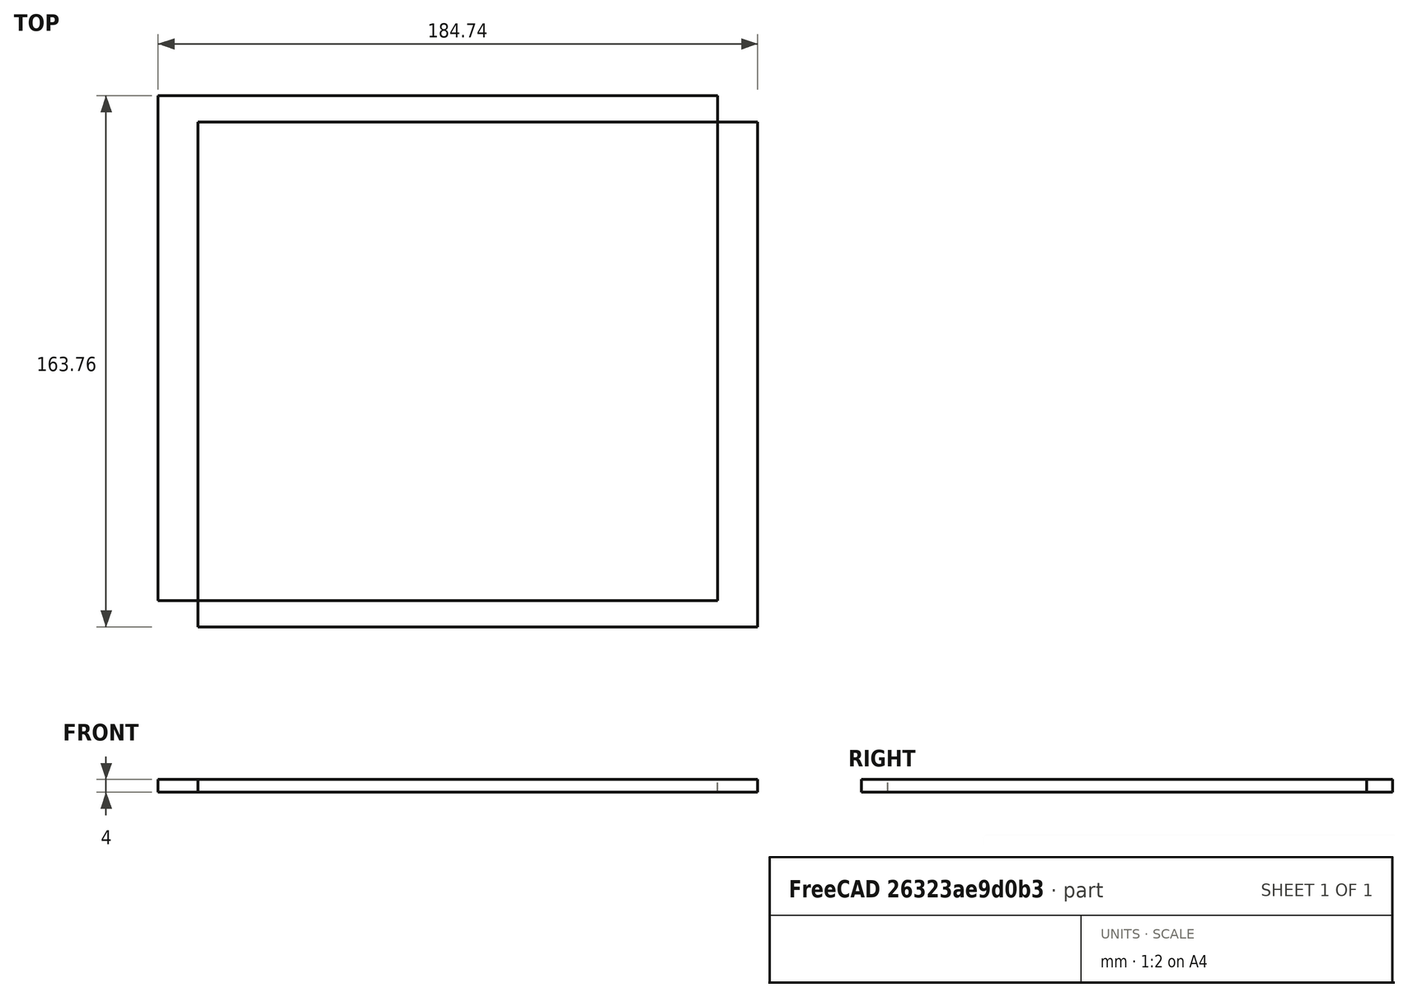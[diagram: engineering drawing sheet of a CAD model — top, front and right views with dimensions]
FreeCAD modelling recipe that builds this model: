
FCSTD DOCUMENT  (FreeCAD 0.19R22922 (Git))
Label: base
License: All rights reserved
LicenseURL: http://en.wikipedia.org/wiki/All_rights_reserved
objects: Path::FeaturePython×6, Sketcher::SketchObject×4, Part::FeaturePython×3, PartDesign::Pad×2, PartDesign::Pocket×2, Part::Feature×1, PartDesign::Fillet×1, PartDesign::Body×1, App::FeaturePython×1, App::DocumentObjectGroup×1, Path::FeatureCompoundPython×1, Mesh::FeaturePython×1
note: 21 computed .brp shape members not serialized (recipe doc carries the construction recipe); baked Part::Feature solids carry a one-line shape summary decoded from their .brp

FEATURE [Part::Feature] path888
  shape: bbox 153.6 x 170.4 x 2e-07 mm, 1 faces, 0 solids (baked)
FEATURE [Sketcher::SketchObject] Sketch
  MapMode = 5
  Support = -> [XY_Plane]
  sketch-geometry (193):
    g0: BSplineCurve PolesCount=2 KnotsCount=2 Degree=1 IsPeriodic=0
    g1: BSplineCurve PolesCount=2 KnotsCount=2 Degree=1 IsPeriodic=0
    g2: BSplineCurve PolesCount=2 KnotsCount=2 Degree=1 IsPeriodic=0
    g3: BSplineCurve PolesCount=2 KnotsCount=2 Degree=1 IsPeriodic=0
    g4: BSplineCurve PolesCount=2 KnotsCount=2 Degree=1 IsPeriodic=0
    g5: BSplineCurve PolesCount=2 KnotsCount=2 Degree=1 IsPeriodic=0
    g6: BSplineCurve PolesCount=2 KnotsCount=2 Degree=1 IsPeriodic=0
    g7: BSplineCurve PolesCount=2 KnotsCount=2 Degree=1 IsPeriodic=0
    g8: BSplineCurve PolesCount=2 KnotsCount=2 Degree=1 IsPeriodic=0
    g9: BSplineCurve PolesCount=2 KnotsCount=2 Degree=1 IsPeriodic=0
    g10: BSplineCurve PolesCount=2 KnotsCount=2 Degree=1 IsPeriodic=0
    g11: BSplineCurve PolesCount=2 KnotsCount=2 Degree=1 IsPeriodic=0
    g12: BSplineCurve PolesCount=2 KnotsCount=2 Degree=1 IsPeriodic=0
    g13: BSplineCurve PolesCount=2 KnotsCount=2 Degree=1 IsPeriodic=0
    g14: BSplineCurve PolesCount=2 KnotsCount=2 Degree=1 IsPeriodic=0
    g15: BSplineCurve PolesCount=2 KnotsCount=2 Degree=1 IsPeriodic=0
    g16: BSplineCurve PolesCount=2 KnotsCount=2 Degree=1 IsPeriodic=0
    g17: BSplineCurve PolesCount=2 KnotsCount=2 Degree=1 IsPeriodic=0
    g18: BSplineCurve PolesCount=2 KnotsCount=2 Degree=1 IsPeriodic=0
    g19: BSplineCurve PolesCount=2 KnotsCount=2 Degree=1 IsPeriodic=0
    g20: BSplineCurve PolesCount=2 KnotsCount=2 Degree=1 IsPeriodic=0
    g21: BSplineCurve PolesCount=2 KnotsCount=2 Degree=1 IsPeriodic=0
    g22: BSplineCurve PolesCount=2 KnotsCount=2 Degree=1 IsPeriodic=0
    g23: BSplineCurve PolesCount=2 KnotsCount=2 Degree=1 IsPeriodic=0
    g24: BSplineCurve PolesCount=2 KnotsCount=2 Degree=1 IsPeriodic=0
    g25: BSplineCurve PolesCount=2 KnotsCount=2 Degree=1 IsPeriodic=0
    g26: BSplineCurve PolesCount=2 KnotsCount=2 Degree=1 IsPeriodic=0
    g27: BSplineCurve PolesCount=2 KnotsCount=2 Degree=1 IsPeriodic=0
    g28: BSplineCurve PolesCount=2 KnotsCount=2 Degree=1 IsPeriodic=0
    g29: BSplineCurve PolesCount=2 KnotsCount=2 Degree=1 IsPeriodic=0
    g30: BSplineCurve PolesCount=2 KnotsCount=2 Degree=1 IsPeriodic=0
    g31: BSplineCurve PolesCount=2 KnotsCount=2 Degree=1 IsPeriodic=0
    g32: BSplineCurve PolesCount=2 KnotsCount=2 Degree=1 IsPeriodic=0
    g33: BSplineCurve PolesCount=2 KnotsCount=2 Degree=1 IsPeriodic=0
    g34: BSplineCurve PolesCount=2 KnotsCount=2 Degree=1 IsPeriodic=0
    g35: BSplineCurve PolesCount=2 KnotsCount=2 Degree=1 IsPeriodic=0
    g36: BSplineCurve PolesCount=2 KnotsCount=2 Degree=1 IsPeriodic=0
    g37: BSplineCurve PolesCount=2 KnotsCount=2 Degree=1 IsPeriodic=0
    g38: BSplineCurve PolesCount=2 KnotsCount=2 Degree=1 IsPeriodic=0
    g39: BSplineCurve PolesCount=2 KnotsCount=2 Degree=1 IsPeriodic=0
    g40: BSplineCurve PolesCount=2 KnotsCount=2 Degree=1 IsPeriodic=0
    g41: BSplineCurve PolesCount=2 KnotsCount=2 Degree=1 IsPeriodic=0
    g42: BSplineCurve PolesCount=2 KnotsCount=2 Degree=1 IsPeriodic=0
    g43: BSplineCurve PolesCount=2 KnotsCount=2 Degree=1 IsPeriodic=0
    g44: BSplineCurve PolesCount=2 KnotsCount=2 Degree=1 IsPeriodic=0
    g45: BSplineCurve PolesCount=2 KnotsCount=2 Degree=1 IsPeriodic=0
    g46: BSplineCurve PolesCount=2 KnotsCount=2 Degree=1 IsPeriodic=0
    g47: BSplineCurve PolesCount=2 KnotsCount=2 Degree=1 IsPeriodic=0
    g48: BSplineCurve PolesCount=2 KnotsCount=2 Degree=1 IsPeriodic=0
    g49: BSplineCurve PolesCount=2 KnotsCount=2 Degree=1 IsPeriodic=0
    g50: BSplineCurve PolesCount=2 KnotsCount=2 Degree=1 IsPeriodic=0
    g51: BSplineCurve PolesCount=2 KnotsCount=2 Degree=1 IsPeriodic=0
    g52: BSplineCurve PolesCount=2 KnotsCount=2 Degree=1 IsPeriodic=0
    g53: BSplineCurve PolesCount=2 KnotsCount=2 Degree=1 IsPeriodic=0
    g54: BSplineCurve PolesCount=2 KnotsCount=2 Degree=1 IsPeriodic=0
    g55: BSplineCurve PolesCount=2 KnotsCount=2 Degree=1 IsPeriodic=0
    g56: BSplineCurve PolesCount=2 KnotsCount=2 Degree=1 IsPeriodic=0
    g57: BSplineCurve PolesCount=2 KnotsCount=2 Degree=1 IsPeriodic=0
    g58: BSplineCurve PolesCount=2 KnotsCount=2 Degree=1 IsPeriodic=0
    g59: BSplineCurve PolesCount=2 KnotsCount=2 Degree=1 IsPeriodic=0
    g60: BSplineCurve PolesCount=2 KnotsCount=2 Degree=1 IsPeriodic=0
    g61: BSplineCurve PolesCount=2 KnotsCount=2 Degree=1 IsPeriodic=0
    g62: BSplineCurve PolesCount=2 KnotsCount=2 Degree=1 IsPeriodic=0
    g63: BSplineCurve PolesCount=2 KnotsCount=2 Degree=1 IsPeriodic=0
    g64: BSplineCurve PolesCount=2 KnotsCount=2 Degree=1 IsPeriodic=0
    g65: BSplineCurve PolesCount=2 KnotsCount=2 Degree=1 IsPeriodic=0
    g66: BSplineCurve PolesCount=2 KnotsCount=2 Degree=1 IsPeriodic=0
    g67: BSplineCurve PolesCount=2 KnotsCount=2 Degree=1 IsPeriodic=0
    g68: BSplineCurve PolesCount=2 KnotsCount=2 Degree=1 IsPeriodic=0
    g69: BSplineCurve PolesCount=2 KnotsCount=2 Degree=1 IsPeriodic=0
    g70: BSplineCurve PolesCount=2 KnotsCount=2 Degree=1 IsPeriodic=0
    g71: BSplineCurve PolesCount=2 KnotsCount=2 Degree=1 IsPeriodic=0
    g72: BSplineCurve PolesCount=2 KnotsCount=2 Degree=1 IsPeriodic=0
    g73: BSplineCurve PolesCount=2 KnotsCount=2 Degree=1 IsPeriodic=0
    g74: BSplineCurve PolesCount=2 KnotsCount=2 Degree=1 IsPeriodic=0
    g75: BSplineCurve PolesCount=2 KnotsCount=2 Degree=1 IsPeriodic=0
    g76: BSplineCurve PolesCount=2 KnotsCount=2 Degree=1 IsPeriodic=0
    g77: BSplineCurve PolesCount=2 KnotsCount=2 Degree=1 IsPeriodic=0
    g78: BSplineCurve PolesCount=2 KnotsCount=2 Degree=1 IsPeriodic=0
    g79: BSplineCurve PolesCount=2 KnotsCount=2 Degree=1 IsPeriodic=0
    g80: BSplineCurve PolesCount=2 KnotsCount=2 Degree=1 IsPeriodic=0
    g81: BSplineCurve PolesCount=2 KnotsCount=2 Degree=1 IsPeriodic=0
    g82: BSplineCurve PolesCount=2 KnotsCount=2 Degree=1 IsPeriodic=0
    g83: BSplineCurve PolesCount=2 KnotsCount=2 Degree=1 IsPeriodic=0
    g84: BSplineCurve PolesCount=2 KnotsCount=2 Degree=1 IsPeriodic=0
    g85: BSplineCurve PolesCount=2 KnotsCount=2 Degree=1 IsPeriodic=0
    g86: BSplineCurve PolesCount=2 KnotsCount=2 Degree=1 IsPeriodic=0
    g87: BSplineCurve PolesCount=2 KnotsCount=2 Degree=1 IsPeriodic=0
    g88: BSplineCurve PolesCount=2 KnotsCount=2 Degree=1 IsPeriodic=0
    g89: BSplineCurve PolesCount=2 KnotsCount=2 Degree=1 IsPeriodic=0
    g90: BSplineCurve PolesCount=2 KnotsCount=2 Degree=1 IsPeriodic=0
    g91: BSplineCurve PolesCount=2 KnotsCount=2 Degree=1 IsPeriodic=0
    g92: BSplineCurve PolesCount=2 KnotsCount=2 Degree=1 IsPeriodic=0
    g93: BSplineCurve PolesCount=2 KnotsCount=2 Degree=1 IsPeriodic=0
    g94: BSplineCurve PolesCount=2 KnotsCount=2 Degree=1 IsPeriodic=0
    g95: BSplineCurve PolesCount=2 KnotsCount=2 Degree=1 IsPeriodic=0
    g96: BSplineCurve PolesCount=2 KnotsCount=2 Degree=1 IsPeriodic=0
    g97: BSplineCurve PolesCount=2 KnotsCount=2 Degree=1 IsPeriodic=0
    g98: BSplineCurve PolesCount=2 KnotsCount=2 Degree=1 IsPeriodic=0
    g99: BSplineCurve PolesCount=2 KnotsCount=2 Degree=1 IsPeriodic=0
    g100: BSplineCurve PolesCount=2 KnotsCount=2 Degree=1 IsPeriodic=0
    g101: BSplineCurve PolesCount=2 KnotsCount=2 Degree=1 IsPeriodic=0
    g102: BSplineCurve PolesCount=2 KnotsCount=2 Degree=1 IsPeriodic=0
    g103: BSplineCurve PolesCount=2 KnotsCount=2 Degree=1 IsPeriodic=0
    g104: BSplineCurve PolesCount=2 KnotsCount=2 Degree=1 IsPeriodic=0
    g105: BSplineCurve PolesCount=2 KnotsCount=2 Degree=1 IsPeriodic=0
    g106: BSplineCurve PolesCount=2 KnotsCount=2 Degree=1 IsPeriodic=0
    g107: BSplineCurve PolesCount=2 KnotsCount=2 Degree=1 IsPeriodic=0
    g108: BSplineCurve PolesCount=2 KnotsCount=2 Degree=1 IsPeriodic=0
    g109: BSplineCurve PolesCount=2 KnotsCount=2 Degree=1 IsPeriodic=0
    g110: BSplineCurve PolesCount=2 KnotsCount=2 Degree=1 IsPeriodic=0
    g111: BSplineCurve PolesCount=2 KnotsCount=2 Degree=1 IsPeriodic=0
    g112: BSplineCurve PolesCount=2 KnotsCount=2 Degree=1 IsPeriodic=0
    g113: BSplineCurve PolesCount=2 KnotsCount=2 Degree=1 IsPeriodic=0
    g114: BSplineCurve PolesCount=2 KnotsCount=2 Degree=1 IsPeriodic=0
    g115: BSplineCurve PolesCount=2 KnotsCount=2 Degree=1 IsPeriodic=0
    g116: BSplineCurve PolesCount=2 KnotsCount=2 Degree=1 IsPeriodic=0
    g117: BSplineCurve PolesCount=2 KnotsCount=2 Degree=1 IsPeriodic=0
    g118: BSplineCurve PolesCount=2 KnotsCount=2 Degree=1 IsPeriodic=0
    g119: BSplineCurve PolesCount=2 KnotsCount=2 Degree=1 IsPeriodic=0
    g120: BSplineCurve PolesCount=2 KnotsCount=2 Degree=1 IsPeriodic=0
    g121: BSplineCurve PolesCount=2 KnotsCount=2 Degree=1 IsPeriodic=0
    g122: BSplineCurve PolesCount=2 KnotsCount=2 Degree=1 IsPeriodic=0
    g123: BSplineCurve PolesCount=2 KnotsCount=2 Degree=1 IsPeriodic=0
    g124: BSplineCurve PolesCount=2 KnotsCount=2 Degree=1 IsPeriodic=0
    g125: BSplineCurve PolesCount=2 KnotsCount=2 Degree=1 IsPeriodic=0
    g126: BSplineCurve PolesCount=2 KnotsCount=2 Degree=1 IsPeriodic=0
    g127: BSplineCurve PolesCount=2 KnotsCount=2 Degree=1 IsPeriodic=0
    g128: BSplineCurve PolesCount=2 KnotsCount=2 Degree=1 IsPeriodic=0
    g129: BSplineCurve PolesCount=2 KnotsCount=2 Degree=1 IsPeriodic=0
    g130: BSplineCurve PolesCount=2 KnotsCount=2 Degree=1 IsPeriodic=0
    g131: BSplineCurve PolesCount=2 KnotsCount=2 Degree=1 IsPeriodic=0
    g132: BSplineCurve PolesCount=2 KnotsCount=2 Degree=1 IsPeriodic=0
    g133: BSplineCurve PolesCount=2 KnotsCount=2 Degree=1 IsPeriodic=0
    g134: BSplineCurve PolesCount=2 KnotsCount=2 Degree=1 IsPeriodic=0
    g135: BSplineCurve PolesCount=2 KnotsCount=2 Degree=1 IsPeriodic=0
    g136: BSplineCurve PolesCount=2 KnotsCount=2 Degree=1 IsPeriodic=0
    g137: BSplineCurve PolesCount=2 KnotsCount=2 Degree=1 IsPeriodic=0
    g138: BSplineCurve PolesCount=2 KnotsCount=2 Degree=1 IsPeriodic=0
    g139: BSplineCurve PolesCount=2 KnotsCount=2 Degree=1 IsPeriodic=0
    g140: BSplineCurve PolesCount=2 KnotsCount=2 Degree=1 IsPeriodic=0
    g141: BSplineCurve PolesCount=2 KnotsCount=2 Degree=1 IsPeriodic=0
    g142: BSplineCurve PolesCount=2 KnotsCount=2 Degree=1 IsPeriodic=0
    g143: BSplineCurve PolesCount=2 KnotsCount=2 Degree=1 IsPeriodic=0
    g144: BSplineCurve PolesCount=2 KnotsCount=2 Degree=1 IsPeriodic=0
    g145: BSplineCurve PolesCount=2 KnotsCount=2 Degree=1 IsPeriodic=0
    g146: BSplineCurve PolesCount=2 KnotsCount=2 Degree=1 IsPeriodic=0
    g147: BSplineCurve PolesCount=2 KnotsCount=2 Degree=1 IsPeriodic=0
    g148: BSplineCurve PolesCount=2 KnotsCount=2 Degree=1 IsPeriodic=0
    g149: BSplineCurve PolesCount=2 KnotsCount=2 Degree=1 IsPeriodic=0
    g150: BSplineCurve PolesCount=2 KnotsCount=2 Degree=1 IsPeriodic=0
    g151: BSplineCurve PolesCount=2 KnotsCount=2 Degree=1 IsPeriodic=0
    g152: BSplineCurve PolesCount=2 KnotsCount=2 Degree=1 IsPeriodic=0
    g153: BSplineCurve PolesCount=2 KnotsCount=2 Degree=1 IsPeriodic=0
    g154: BSplineCurve PolesCount=2 KnotsCount=2 Degree=1 IsPeriodic=0
    g155: BSplineCurve PolesCount=2 KnotsCount=2 Degree=1 IsPeriodic=0
    g156: BSplineCurve PolesCount=2 KnotsCount=2 Degree=1 IsPeriodic=0
    g157: BSplineCurve PolesCount=2 KnotsCount=2 Degree=1 IsPeriodic=0
    g158: BSplineCurve PolesCount=2 KnotsCount=2 Degree=1 IsPeriodic=0
    g159: BSplineCurve PolesCount=2 KnotsCount=2 Degree=1 IsPeriodic=0
    g160: BSplineCurve PolesCount=2 KnotsCount=2 Degree=1 IsPeriodic=0
    g161: BSplineCurve PolesCount=2 KnotsCount=2 Degree=1 IsPeriodic=0
    g162: BSplineCurve PolesCount=2 KnotsCount=2 Degree=1 IsPeriodic=0
    g163: BSplineCurve PolesCount=2 KnotsCount=2 Degree=1 IsPeriodic=0
    g164: BSplineCurve PolesCount=2 KnotsCount=2 Degree=1 IsPeriodic=0
    g165: BSplineCurve PolesCount=2 KnotsCount=2 Degree=1 IsPeriodic=0
    g166: BSplineCurve PolesCount=2 KnotsCount=2 Degree=1 IsPeriodic=0
    g167: BSplineCurve PolesCount=2 KnotsCount=2 Degree=1 IsPeriodic=0
    g168: BSplineCurve PolesCount=2 KnotsCount=2 Degree=1 IsPeriodic=0
    g169: BSplineCurve PolesCount=2 KnotsCount=2 Degree=1 IsPeriodic=0
    g170: BSplineCurve PolesCount=2 KnotsCount=2 Degree=1 IsPeriodic=0
    g171: BSplineCurve PolesCount=2 KnotsCount=2 Degree=1 IsPeriodic=0
    g172: BSplineCurve PolesCount=2 KnotsCount=2 Degree=1 IsPeriodic=0
    g173: BSplineCurve PolesCount=2 KnotsCount=2 Degree=1 IsPeriodic=0
    g174: BSplineCurve PolesCount=2 KnotsCount=2 Degree=1 IsPeriodic=0
    g175: BSplineCurve PolesCount=2 KnotsCount=2 Degree=1 IsPeriodic=0
    g176: BSplineCurve PolesCount=2 KnotsCount=2 Degree=1 IsPeriodic=0
    g177: BSplineCurve PolesCount=2 KnotsCount=2 Degree=1 IsPeriodic=0
    g178: BSplineCurve PolesCount=2 KnotsCount=2 Degree=1 IsPeriodic=0
    g179: BSplineCurve PolesCount=2 KnotsCount=2 Degree=1 IsPeriodic=0
    g180: BSplineCurve PolesCount=2 KnotsCount=2 Degree=1 IsPeriodic=0
    g181: BSplineCurve PolesCount=2 KnotsCount=2 Degree=1 IsPeriodic=0
    g182: BSplineCurve PolesCount=2 KnotsCount=2 Degree=1 IsPeriodic=0
    g183: BSplineCurve PolesCount=2 KnotsCount=2 Degree=1 IsPeriodic=0
    g184: BSplineCurve PolesCount=2 KnotsCount=2 Degree=1 IsPeriodic=0
    g185: BSplineCurve PolesCount=2 KnotsCount=2 Degree=1 IsPeriodic=0
    g186: BSplineCurve PolesCount=2 KnotsCount=2 Degree=1 IsPeriodic=0
    g187: BSplineCurve PolesCount=2 KnotsCount=2 Degree=1 IsPeriodic=0
    g188: BSplineCurve PolesCount=2 KnotsCount=2 Degree=1 IsPeriodic=0
    g189: BSplineCurve PolesCount=2 KnotsCount=2 Degree=1 IsPeriodic=0
    g190: BSplineCurve PolesCount=2 KnotsCount=2 Degree=1 IsPeriodic=0
    g191: BSplineCurve PolesCount=2 KnotsCount=2 Degree=1 IsPeriodic=0
    g192: BSplineCurve PolesCount=2 KnotsCount=2 Degree=1 IsPeriodic=0
  constraints (193):
    c: Coincident(g0,g1)
    c: Coincident(g1,g2)
    c: Coincident(g2,g3)
    c: Coincident(g3,g4)
    c: Coincident(g4,g5)
    c: Coincident(g5,g6)
    c: Coincident(g6,g7)
    c: Coincident(g7,g8)
    c: Coincident(g8,g9)
    c: Coincident(g9,g10)
    c: Coincident(g10,g11)
    c: Coincident(g11,g12)
    c: Coincident(g12,g13)
    c: Coincident(g13,g14)
    c: Coincident(g14,g15)
    c: Coincident(g15,g16)
    c: Coincident(g16,g17)
    c: Coincident(g17,g18)
    c: Coincident(g18,g19)
    c: Coincident(g19,g20)
    c: Coincident(g20,g21)
    c: Coincident(g21,g22)
    c: Coincident(g22,g23)
    c: Coincident(g23,g24)
    c: Coincident(g24,g25)
    c: Coincident(g25,g26)
    c: Coincident(g26,g27)
    c: Coincident(g27,g28)
    c: Coincident(g28,g29)
    c: Coincident(g29,g30)
    c: Coincident(g30,g31)
    c: Coincident(g31,g32)
    c: Coincident(g32,g33)
    c: Coincident(g33,g34)
    c: Coincident(g34,g35)
    c: Coincident(g35,g36)
    c: Coincident(g36,g37)
    c: Coincident(g37,g38)
    c: Coincident(g38,g39)
    c: Coincident(g39,g40)
    c: Coincident(g40,g41)
    c: Coincident(g41,g42)
    c: Coincident(g42,g43)
    c: Coincident(g43,g44)
    c: Coincident(g44,g45)
    c: Coincident(g45,g46)
    c: Coincident(g46,g47)
    c: Coincident(g47,g48)
    c: Coincident(g48,g49)
    c: Coincident(g49,g50)
    c: Coincident(g50,g51)
    c: Coincident(g51,g52)
    c: Coincident(g52,g53)
    c: Coincident(g53,g54)
    c: Coincident(g54,g55)
    c: Coincident(g55,g56)
    c: Coincident(g56,g57)
    c: Coincident(g57,g58)
    c: Coincident(g58,g59)
    c: Coincident(g59,g60)
    c: Coincident(g60,g61)
    c: Coincident(g61,g62)
    c: Coincident(g62,g63)
    c: Coincident(g63,g64)
    c: Coincident(g64,g65)
    c: Coincident(g65,g66)
    c: Coincident(g66,g67)
    c: Coincident(g67,g68)
    c: Coincident(g68,g69)
    c: Coincident(g69,g70)
    c: Coincident(g70,g71)
    c: Coincident(g71,g72)
    c: Coincident(g72,g73)
    c: Coincident(g73,g74)
    c: Coincident(g74,g75)
    c: Coincident(g75,g76)
    c: Coincident(g76,g77)
    c: Coincident(g77,g78)
    c: Coincident(g78,g79)
    c: Coincident(g79,g80)
    c: Coincident(g80,g81)
    c: Coincident(g81,g82)
    c: Coincident(g82,g83)
    c: Coincident(g83,g84)
    c: Coincident(g84,g85)
    c: Coincident(g85,g86)
    c: Coincident(g86,g87)
    c: Coincident(g87,g88)
    c: Coincident(g88,g89)
    c: Coincident(g89,g90)
    c: Coincident(g90,g91)
    c: Coincident(g91,g92)
    c: Coincident(g92,g93)
    c: Coincident(g93,g94)
    c: Coincident(g94,g95)
    c: Coincident(g95,g96)
    c: Coincident(g96,g97)
    c: Coincident(g97,g98)
    c: Coincident(g98,g99)
    c: Coincident(g99,g100)
    c: Coincident(g100,g101)
    c: Coincident(g101,g102)
    c: Coincident(g102,g103)
    c: Coincident(g103,g104)
    c: Coincident(g104,g105)
    c: Coincident(g105,g106)
    c: Coincident(g106,g107)
    c: Coincident(g107,g108)
    c: Coincident(g108,g109)
    c: Coincident(g109,g110)
    c: Coincident(g110,g111)
    c: Coincident(g111,g112)
    c: Coincident(g112,g113)
    c: Coincident(g113,g114)
    c: Coincident(g114,g115)
    c: Coincident(g115,g116)
    c: Coincident(g116,g117)
    c: Coincident(g117,g118)
    c: Coincident(g118,g119)
    c: Coincident(g119,g120)
    c: Coincident(g120,g121)
    c: Coincident(g121,g122)
    c: Coincident(g122,g123)
    c: Coincident(g123,g124)
    c: Coincident(g124,g125)
    c: Coincident(g125,g126)
    c: Coincident(g126,g127)
    c: Coincident(g127,g128)
    c: Coincident(g128,g129)
    c: Coincident(g129,g130)
    c: Coincident(g130,g131)
    c: Coincident(g131,g132)
    c: Coincident(g132,g133)
    c: Coincident(g133,g134)
    c: Coincident(g134,g135)
    c: Coincident(g135,g136)
    c: Coincident(g136,g137)
    c: Coincident(g137,g138)
    c: Coincident(g138,g139)
    c: Coincident(g139,g140)
    c: Coincident(g140,g141)
    c: Coincident(g141,g142)
    c: Coincident(g142,g143)
    c: Coincident(g143,g144)
    c: Coincident(g144,g145)
    c: Coincident(g145,g146)
    c: Coincident(g146,g147)
    c: Coincident(g147,g148)
    c: Coincident(g148,g149)
    c: Coincident(g149,g150)
    c: Coincident(g150,g151)
    c: Coincident(g151,g152)
    c: Coincident(g152,g153)
    c: Coincident(g153,g154)
    c: Coincident(g154,g155)
    c: Coincident(g155,g156)
    c: Coincident(g156,g157)
    c: Coincident(g157,g158)
    c: Coincident(g158,g159)
    c: Coincident(g159,g160)
    c: Coincident(g160,g161)
    c: Coincident(g161,g162)
    c: Coincident(g162,g163)
    c: Coincident(g163,g164)
    c: Coincident(g164,g165)
    c: Coincident(g165,g166)
    c: Coincident(g166,g167)
    c: Coincident(g167,g168)
    c: Coincident(g168,g169)
    c: Coincident(g169,g170)
    c: Coincident(g170,g171)
    c: Coincident(g171,g172)
    c: Coincident(g172,g173)
    c: Coincident(g173,g174)
    c: Coincident(g174,g175)
    c: Coincident(g175,g176)
    c: Coincident(g176,g177)
    c: Coincident(g177,g178)
    c: Coincident(g178,g179)
    c: Coincident(g179,g180)
    c: Coincident(g180,g181)
    c: Coincident(g181,g182)
    c: Coincident(g182,g183)
    c: Coincident(g183,g184)
    c: Coincident(g184,g185)
    c: Coincident(g185,g186)
    c: Coincident(g186,g187)
    c: Coincident(g187,g188)
    c: Coincident(g188,g189)
    c: Coincident(g189,g190)
    c: Coincident(g190,g191)
    c: Coincident(g191,g192)
    c: Coincident(g192,g0)
FEATURE [PartDesign::Pad] Pad
  Direction = (1,1,1)
  Length = 4
  Length2 = 100
  Profile = -> Sketch
  Type = 0
FEATURE [Sketcher::SketchObject] Sketch001
  MapMode = 5
  Placement = pos=(0,0,4) rot=(0,0,1;0rad)
  Support = -> [Pad]
  sketch-geometry (4):
    g0: LineSegment StartX=82 StartY=138 StartZ=0 EndX=144 EndY=138 EndZ=0
    g1: LineSegment StartX=144 StartY=138 StartZ=0 EndX=144 EndY=76 EndZ=0
    g2: LineSegment StartX=144 StartY=76 StartZ=0 EndX=82 EndY=76 EndZ=0
    g3: LineSegment StartX=82 StartY=76 StartZ=0 EndX=82 EndY=138 EndZ=0
  constraints (12):
    c: Coincident(g0,g1)
    c: Coincident(g1,g2)
    c: Coincident(g2,g3)
    c: Coincident(g3,g0)
    c: Horizontal(g0)
    c: Horizontal(g2)
    c: Vertical(g1)
    c: Vertical(g3)
    c: Equal(g0,g1)
    c: DistanceX(g0,g0) = 62
    c: DistanceX(g-1,g2) = 82
    c: DistanceY(g2) = 76
FEATURE [PartDesign::Pocket] Pocket
  BaseFeature = -> Pad
  Length = 3
  Length2 = 100
  Profile = -> Sketch001
  Type = 0
FEATURE [Sketcher::SketchObject] Sketch002
  ExternalGeometry = -> [Pocket]
  MapMode = 5
  Placement = pos=(0,0,1) rot=(0,0,1;0rad)
  Support = -> [Pocket]
  expr: Constraints[15] = (62 - 49.53) / 2
  expr: Constraints[14] = (62 - 49.53) / 2
  sketch-geometry (6):
    g0: Circle CenterX=88.235 CenterY=131.765 CenterZ=0 NormalX=0 NormalY=0 NormalZ=1 AngleXU=0 Radius=1.5
    g1: Circle CenterX=137.765 CenterY=131.765 CenterZ=0 NormalX=0 NormalY=0 NormalZ=1 AngleXU=0 Radius=1.5
    g2: Circle CenterX=137.765 CenterY=82.235 CenterZ=0 NormalX=0 NormalY=0 NormalZ=1 AngleXU=0 Radius=1.5
    g3: Circle CenterX=88.235 CenterY=82.235 CenterZ=0 NormalX=0 NormalY=0 NormalZ=1 AngleXU=0 Radius=1.5
    g4: LineSegment [constr] StartX=88.235 StartY=131.765 StartZ=0 EndX=137.765 EndY=131.765 EndZ=0
    g5: LineSegment [constr] StartX=137.765 StartY=131.765 StartZ=0 EndX=137.765 EndY=82.235 EndZ=0
  constraints (16):
    c: Equal(g0,g1)
    c: Equal(g1,g2)
    c: Equal(g2,g3)
    c: Diameter(g0) = 3
    c: Vertical(g3,g0)
    c: Horizontal(g3,g2)
    c: Coincident(g4,g0)
    c: Coincident(g4,g1)
    c: Horizontal(g4)
    c: Coincident(g5,g1)
    c: Coincident(g5,g2)
    c: Vertical(g5)
    c: Equal(g4,g5)
    c: DistanceX(g4,g4) = 49.53
    c: DistanceX(g-3,g0) = 6.235
    c: DistanceY(g0,g-3) = 6.235
FEATURE [PartDesign::Pad] Pad001
  BaseFeature = -> Pocket
  Direction = (1,1,1)
  Length = 3
  Length2 = 100
  Profile = -> Sketch002
  Type = 0
FEATURE [Sketcher::SketchObject] Sketch003
  ExternalGeometry = -> [Pad001]
  MapMode = 5
  Support = -> [XY_Plane]
  sketch-geometry (10):
    g0: Circle CenterX=66.0713 CenterY=172.15 CenterZ=0 NormalX=0 NormalY=0 NormalZ=1 AngleXU=0 Radius=1.5875
    g1: Circle CenterX=145.398 CenterY=152.575 CenterZ=0 NormalX=0 NormalY=0 NormalZ=1 AngleXU=0 Radius=1.5875
    g2: Circle CenterX=85.3151 CenterY=42.3534 CenterZ=0 NormalX=0 NormalY=0 NormalZ=1 AngleXU=0 Radius=1.5875
    g3: Circle CenterX=11.0869 CenterY=123.341 CenterZ=0 NormalX=0 NormalY=0 NormalZ=1 AngleXU=0 Radius=1.5875
    g4: Circle CenterX=145.252 CenterY=65.6752 CenterZ=0 NormalX=0 NormalY=0 NormalZ=1 AngleXU=0 Radius=1.5875
    g5: Circle [constr] CenterX=66.0713 CenterY=172.15 CenterZ=0 NormalX=0 NormalY=0 NormalZ=1 AngleXU=0 Radius=4
    g6: Circle [constr] CenterX=145.398 CenterY=152.575 CenterZ=0 NormalX=0 NormalY=0 NormalZ=1 AngleXU=0 Radius=4
    g7: Circle [constr] CenterX=145.252 CenterY=65.6752 CenterZ=0 NormalX=0 NormalY=0 NormalZ=1 AngleXU=0 Radius=4
    g8: Circle [constr] CenterX=85.3151 CenterY=42.3534 CenterZ=0 NormalX=0 NormalY=0 NormalZ=1 AngleXU=0 Radius=4
    g9: Circle [constr] CenterX=11.0869 CenterY=123.341 CenterZ=0 NormalX=0 NormalY=0 NormalZ=1 AngleXU=0 Radius=4
  constraints (15):
    c: Equal(g0,g1)
    c: Equal(g1,g3)
    c: Equal(g3,g4)
    c: Equal(g4,g2)
    c: Diameter(g0) = 3.175
    c: Coincident(g5,g0)
    c: Diameter(g5) = 8
    c: Coincident(g6,g1)
    c: Diameter(g6) = 8
    c: Coincident(g7,g4)
    c: Diameter(g7) = 8
    c: Coincident(g8,g2)
    c: Diameter(g8) = 8
    c: Coincident(g9,g3)
    c: Diameter(g9) = 8
FEATURE [PartDesign::Pocket] Pocket001
  BaseFeature = -> Pad001
  Length = 4
  Length2 = 100
  Profile = -> Sketch003
  Reversed = true
  Type = 1
FEATURE [PartDesign::Fillet] Fillet
  Base = -> Pocket001 [Edge604,Edge600,Edge599,Edge602]
  BaseFeature = -> Pocket001
  Radius = 5
  SupportTransform = false
FEATURE [PartDesign::Body] Body
  Group = -> [Sketch,Pad,Sketch001,Pocket,Sketch002,Pad001,Sketch003,Pocket001,Fillet]
  Origin = -> Origin
  Placement = pos=(-10,-5,-4) rot=(0,0,1;0rad)
  Tip = -> Fillet
FEATURE [App::FeaturePython] SetupSheet  # Path/CAM operation (typed FeaturePython)
  ClearanceHeightExpression = OpStockZMax+SetupSheet.ClearanceHeightOffset
  ClearanceHeightOffset = 5
  CoolantMode = 0
  CoolantModes = None | Flood | Mist
  FinalDepthExpression = OpFinalDepth
  HorizRapid = 10
  SafeHeightExpression = OpStockZMax+SetupSheet.SafeHeightOffset
  SafeHeightOffset = 3
  StartDepthExpression = OpStartDepth
  StepDownExpression = 1.5
  VertRapid = 10
FEATURE [Part::FeaturePython] Clone  label="Model-Body"  # Draft clone (typed FeaturePython)
  AttacherType = Attacher::AttachEngine3D
  Fuse = false
  Objects = -> [Body]
  PathResource = Model
  Placement = pos=(-4.71876,161.752,-4) rot=(0,0,-1;1.5708rad)
  Scale = (1,1,1)
FEATURE [App::DocumentObjectGroup] Model
  Group = -> [Clone]
FEATURE [Path::FeaturePython] Default_Tool  label="Default Tool"  # Path/CAM operation (typed FeaturePython)
  HorizFeed = 0
  HorizRapid = 10
  SpindleDir = 0
  SpindleSpeed = 0
  ToolNumber = 1
  VertFeed = 0
  VertRapid = 10
  expr: VertRapid = SetupSheet.VertRapid
  expr: HorizRapid = SetupSheet.HorizRapid
FEATURE [Path::FeaturePython] T1__Flat  label="T1: Flat"  # Path/CAM operation (typed FeaturePython)
  HorizFeed = 4
  HorizRapid = 10
  SpindleDir = 0
  SpindleSpeed = 1000
  ToolNumber = 1
  VertFeed = 4
  VertRapid = 10
  expr: VertRapid = SetupSheet.VertRapid
  expr: HorizRapid = SetupSheet.HorizRapid
FEATURE [Path::FeaturePython] Pocket_Shape  # Path/CAM operation (typed FeaturePython)
  Active = true
  AreaParams:
    Tolerance = 1e-07
    FitArcs = True
    Simplify = False
    CleanDistance = 0.0
    Accuracy = 0.01
    Unit = 1.0
    MinArcPoints = 4
    MaxArcPoints = 100
    ClipperScale = 10000000.0
    Fill = 0
    Coplanar = 0
    Reorient = True
    Outline = False
    Explode = False
    OpenMode = 0
    Deflection = 0.01
    SubjectFill = 0
    ClipFill = 0
    Offset = 0.0
    ExtraPass = 0
    Stepover = 0.0
    LastStepover = 0.0
    JoinType = 0
    EndType = 0
    MiterLimit = 2.0
    RoundPrecision = 0.0
    PocketMode = 4
    ToolRadius = 1.585
    PocketExtraOffset = 0.0
    PocketStepover = 1.585
    PocketLastStepover = 0.0
    FromCenter = True
    Angle = 45.0
    AngleShift = 0.0
    Shift = 0.0
    Thicken = False
    SectionCount = -1
    Stepdown = 1.0
    SectionOffset = 0.0
    SectionTolerance = 1e-06
    SectionMode = 2
    Project = False
  AttemptInverseAngle = true
  Base = -> [Clone]
  ClearanceHeight = 5
  CoolantMode = None
  CutMode = 1
  CycleTime = 01:06:53
  EnableRotation = 0
  ExtensionCorners = true
  ExtensionLengthDefault = 1.585
  ExtraOffset = 0
  FinalDepth = -3
  FinishDepth = 0
  InverseAngle = false
  KeepToolDown = false
  LimitDepthToFace = true
  MinTravel = false
  OffsetPattern = 3
  OpFinalDepth = -3
  OpStartDepth = 0
  OpStockZMax = 0
  OpStockZMin = -4
  OpToolDiameter = 3.17
  PathParams = {'orientation': 0, 'feedrate': 4.0, 'feedrate_v': 4.0, 'verbose': True, 'resume_height': 3.0, 'retraction': 5.0, 'return_end': True, 'preamble': False}
  ReverseDirection = false
  SafeHeight = 3
  StartAt = 0
  StartDepth = 0
  StartPoint = (0,0,0)
  StepDown = 0.5
  StepOver = 50
  ToolController = -> T1__Flat
  UseOutline = false
  UseStartPoint = false
  ZigZagAngle = 45
  expr: StartDepth = OpStartDepth
  expr: FinalDepth = OpFinalDepth
  expr: StepDown = 0.5
  expr: SafeHeight = OpStockZMax + SetupSheet.SafeHeightOffset
  expr: ClearanceHeight = OpStockZMax + SetupSheet.ClearanceHeightOffset
  expr: ExtensionLengthDefault = OpToolDiameter / 2
FEATURE [Path::FeaturePython] Profile  # Path/CAM operation (typed FeaturePython)
  Active = true
  AreaParams:
    Tolerance = 1e-07
    FitArcs = True
    Simplify = False
    CleanDistance = 0.0
    Accuracy = 0.01
    Unit = 1.0
    MinArcPoints = 4
    MaxArcPoints = 100
    ClipperScale = 10000000.0
    Fill = 0
    Coplanar = 0
    Reorient = True
    Outline = False
    Explode = False
    OpenMode = 0
    Deflection = 0.01
    SubjectFill = 0
    ClipFill = 0
    Offset = -1.585
    ExtraPass = 0
    Stepover = 0.0
    LastStepover = 0.0
    JoinType = 0
    EndType = 0
    MiterLimit = 2.0
    RoundPrecision = 0.0
    PocketMode = 0
    ToolRadius = 1.0
    PocketExtraOffset = 0.0
    PocketStepover = 0.0
    PocketLastStepover = 0.0
    FromCenter = False
    Angle = 45.0
    AngleShift = 0.0
    Shift = 0.0
    Thicken = False
    SectionCount = -1
    Stepdown = 1.0
    SectionOffset = 0.0
    SectionTolerance = 1e-06
    SectionMode = 2
    Project = False
  AttemptInverseAngle = true
  Base = -> [Clone]
  ClearanceHeight = 5
  CoolantMode = None
  CycleTime = 00:21:12
  Direction = 0
  EnableRotation = 0
  ExpandProfile = 0
  ExpandProfileStepOver = 100
  FinalDepth = -4.5
  HandleMultipleFeatures = 1
  InverseAngle = false
  JoinType = 0
  LimitDepthToFace = true
  MiterLimit = 0.1
  OffsetExtra = 0
  OpFinalDepth = 0
  OpStartDepth = 0.5
  OpStockZMax = 0
  OpStockZMin = -4
  OpToolDiameter = 3.17
  PathParams = {'orientation': 0, 'feedrate': 4.0, 'feedrate_v': 4.0, 'verbose': True, 'resume_height': 3.0, 'retraction': 5.0, 'return_end': True, 'preamble': False, 'start': Vector (0.0, 0.0, 5.0)}
  ReverseDirection = false
  SafeHeight = 3
  Side = 0
  StartDepth = 0
  StartPoint = (0,0,0)
  StepDown = 0.5
  ToolController = -> T1__Flat
  UseComp = true
  UseStartPoint = false
  processCircles = true
  processHoles = false
  processPerimeter = true
  expr: StartDepth = 0
  expr: FinalDepth = -4.5
  expr: StepDown = 0.5
  expr: SafeHeight = OpStockZMax + SetupSheet.SafeHeightOffset
  expr: ClearanceHeight = OpStockZMax + SetupSheet.ClearanceHeightOffset
FEATURE [Path::FeaturePython] Drilling  # Path/CAM operation (typed FeaturePython)
  Active = true
  AddTipLength = false
  AttemptInverseAngle = false
  Base = -> [Clone]
  ClearanceHeight = 5
  CoolantMode = None
  CycleTime = 00:00:04
  DwellEnabled = false
  DwellTime = 1
  EnableRotation = 0
  ExtraOffset = 0
  FinalDepth = -4.5
  InverseAngle = false
  OpFinalDepth = -4
  OpStartDepth = 0
  OpStockZMax = 0
  OpStockZMin = -4
  OpToolDiameter = 3.17
  PeckDepth = 2.3775
  PeckEnabled = false
  RetractHeight = 1
  ReturnLevel = 0
  ReverseDirection = false
  SafeHeight = 3
  StartDepth = 0
  ToolController = -> T1__Flat
  expr: StartDepth = OpStartDepth
  expr: FinalDepth = -4.5
  expr: SafeHeight = OpStockZMax + SetupSheet.SafeHeightOffset
  expr: RetractHeight = OpStartDepth + 1mm
  expr: ClearanceHeight = OpStockZMax + SetupSheet.ClearanceHeightOffset
  expr: PeckDepth = OpToolDiameter * 0.75
FEATURE [Path::FeatureCompoundPython] Operations  # Path/CAM operation (typed FeaturePython)
  Group = -> [Pocket_Shape,Drilling,Profile]
  UsePlacements = false
FEATURE [Part::FeaturePython] Stock001  # WARN: FeaturePython — macro-defined, semantics opaque (R4)
  Base = -> Model
  ExtXneg = 1
  ExtXpos = 1
  ExtYneg = 1
  ExtYpos = 1
  ExtZneg = 0
  ExtZpos = 0
  Placement = pos=(-11.2929,9.1222,-4) rot=(0,0,1;0rad)
  StockType = FromBase
FEATURE [Part::FeaturePython] Stock002  # WARN: FeaturePython — macro-defined, semantics opaque (R4)
  Base = -> Model
  ExtXneg = 1
  ExtXpos = 1
  ExtYneg = 1
  ExtYpos = 1
  ExtZneg = 0
  ExtZpos = 0
  Placement = pos=(1,1,-4) rot=(0,0,1;0rad)
  StockType = FromBase
FEATURE [Path::FeaturePython] Job  # Path/CAM operation (typed FeaturePython)
  CycleTime = 01:28:09
  Fixtures = G54
  GeometryTolerance = 0.01
  LastPostProcessDate = 2020-11-07 16:35:37.970717
  LastPostProcessOutput = <userpath>/projects/ferro-dactyl/freecad/base.gcode
  Model = -> Model
  Operations = -> Operations
  OrderOutputBy = 0
  PostProcessor = 4
  SetupSheet = -> SetupSheet
  SplitOutput = false
  Stock = -> Stock002
  ToolController = -> [Default_Tool,T1__Flat]
FEATURE [Mesh::FeaturePython] CutMaterial  # WARN: FeaturePython — macro-defined, semantics opaque (R4)
